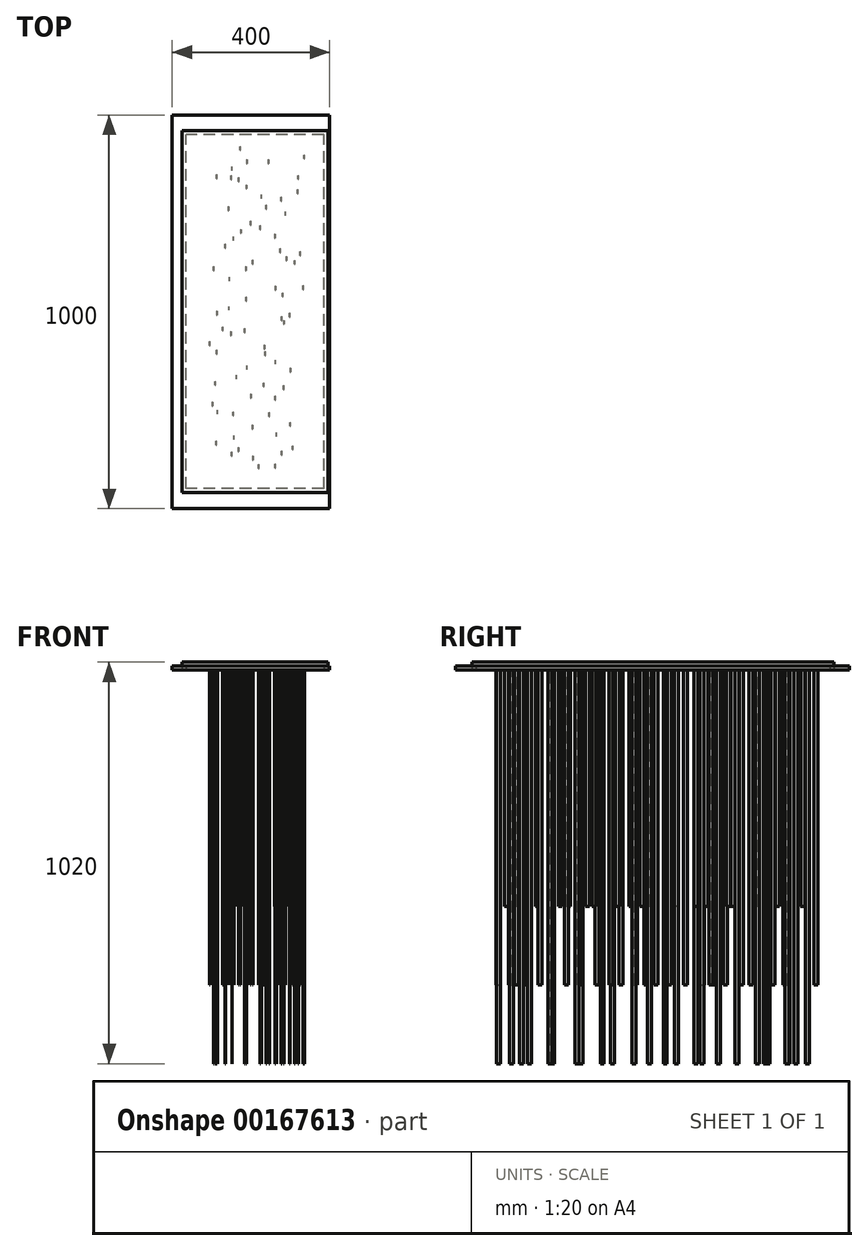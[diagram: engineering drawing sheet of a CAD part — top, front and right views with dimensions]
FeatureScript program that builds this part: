
annotation { "Feature Type Name" : "Feature", "Feature Type Description" : "" }
export const myFeature = defineFeature(function(context is Context, id is Id, definition is map)
    precondition{}
    {
        {
            var Q0;
            Q0=qCreatedBy(makeId("Top.planeOp"),FACE);
            var sketch = newSketch(context, id + "F0", { "sketchPlane" : qUnion([Q0])});
            skLineSegment(sketch, "E0.bottom", {"start": v(225, -500) * mm, "end": v(-225, -500) * mm});
            skLineSegment(sketch, "E0.top", {"start": v(225, 500) * mm, "end": v(-225, 500) * mm});
            skLineSegment(sketch, "E0.left", {"start": v(225, -500) * mm, "end": v(225, 500) * mm});
            skLineSegment(sketch, "E0.right", {"start": v(-225, -500) * mm, "end": v(-225, 500) * mm});
            skPoint(sketch, "E0.middle", {"position": v(0, 0) * mm});
            skSolve(sketch);
        }
        {
            var Q0;
            Q0=qCreatedBy(makeId("Top.planeOp"),FACE);
            var sketch = newSketch(context, id + "F1", { "sketchPlane" : qUnion([Q0])});
            skLineSegment(sketch, "E1.bottom", {"start": v(97.67, -13.3) * mm, "end": v(98.67, -13.3) * mm});
            skLineSegment(sketch, "E1.top", {"start": v(97.67, -3.3) * mm, "end": v(98.67, -3.3) * mm});
            skLineSegment(sketch, "E1.left", {"start": v(97.67, -13.3) * mm, "end": v(97.67, -3.3) * mm});
            skLineSegment(sketch, "E1.right", {"start": v(98.67, -13.3) * mm, "end": v(98.67, -3.3) * mm});
            skLineSegment(sketch, "E2.bottom", {"start": v(-15.97, -52.02) * mm, "end": v(-14.97, -52.02) * mm});
            skLineSegment(sketch, "E2.top", {"start": v(-15.97, -42.02) * mm, "end": v(-14.97, -42.02) * mm});
            skLineSegment(sketch, "E2.left", {"start": v(-15.97, -52.02) * mm, "end": v(-15.97, -42.02) * mm});
            skLineSegment(sketch, "E2.right", {"start": v(-14.97, -52.02) * mm, "end": v(-14.97, -42.02) * mm});
            skLineSegment(sketch, "E3.bottom", {"start": v(-12.36, 27.2) * mm, "end": v(-11.36, 27.2) * mm});
            skLineSegment(sketch, "E3.top", {"start": v(-12.36, 37.2) * mm, "end": v(-11.36, 37.2) * mm});
            skLineSegment(sketch, "E3.left", {"start": v(-12.36, 27.2) * mm, "end": v(-12.36, 37.2) * mm});
            skLineSegment(sketch, "E3.right", {"start": v(-11.36, 27.2) * mm, "end": v(-11.36, 37.2) * mm});
            skLineSegment(sketch, "E4.bottom", {"start": v(-91.45, -186.35) * mm, "end": v(-90.45, -186.35) * mm});
            skLineSegment(sketch, "E4.top", {"start": v(-91.45, -176.35) * mm, "end": v(-90.45, -176.35) * mm});
            skLineSegment(sketch, "E4.left", {"start": v(-91.45, -186.35) * mm, "end": v(-91.45, -176.35) * mm});
            skLineSegment(sketch, "E4.right", {"start": v(-90.45, -186.35) * mm, "end": v(-90.45, -176.35) * mm});
            skLineSegment(sketch, "E5.bottom", {"start": v(-87.84, -107.13) * mm, "end": v(-86.84, -107.13) * mm});
            skLineSegment(sketch, "E5.top", {"start": v(-87.84, -97.13) * mm, "end": v(-86.84, -97.13) * mm});
            skLineSegment(sketch, "E5.left", {"start": v(-87.84, -107.13) * mm, "end": v(-87.84, -97.13) * mm});
            skLineSegment(sketch, "E5.right", {"start": v(-86.84, -107.13) * mm, "end": v(-86.84, -97.13) * mm});
            skLineSegment(sketch, "E6.bottom", {"start": v(83.14, -197.41) * mm, "end": v(84.14, -197.41) * mm});
            skLineSegment(sketch, "E6.top", {"start": v(83.14, -187.41) * mm, "end": v(84.14, -187.41) * mm});
            skLineSegment(sketch, "E6.left", {"start": v(83.14, -197.41) * mm, "end": v(83.14, -187.41) * mm});
            skLineSegment(sketch, "E6.right", {"start": v(84.14, -197.41) * mm, "end": v(84.14, -187.41) * mm});
            skLineSegment(sketch, "E7.bottom", {"start": v(61.74, -132.83) * mm, "end": v(62.74, -132.83) * mm});
            skLineSegment(sketch, "E7.top", {"start": v(61.74, -122.83) * mm, "end": v(62.74, -122.83) * mm});
            skLineSegment(sketch, "E7.left", {"start": v(61.74, -132.83) * mm, "end": v(61.74, -122.83) * mm});
            skLineSegment(sketch, "E7.right", {"start": v(62.74, -132.83) * mm, "end": v(62.74, -122.83) * mm});
            skLineSegment(sketch, "E8.bottom", {"start": v(132.38, 56.37) * mm, "end": v(133.38, 56.37) * mm});
            skLineSegment(sketch, "E8.top", {"start": v(132.38, 66.37) * mm, "end": v(133.38, 66.37) * mm});
            skLineSegment(sketch, "E8.left", {"start": v(132.38, 56.37) * mm, "end": v(132.38, 66.37) * mm});
            skLineSegment(sketch, "E8.right", {"start": v(133.38, 56.37) * mm, "end": v(133.38, 66.37) * mm});
            skLineSegment(sketch, "E9.bottom", {"start": v(110.98, 120.95) * mm, "end": v(111.98, 120.95) * mm});
            skLineSegment(sketch, "E9.top", {"start": v(110.98, 130.95) * mm, "end": v(111.98, 130.95) * mm});
            skLineSegment(sketch, "E9.left", {"start": v(110.98, 120.95) * mm, "end": v(110.98, 130.95) * mm});
            skLineSegment(sketch, "E9.right", {"start": v(111.98, 120.95) * mm, "end": v(111.98, 130.95) * mm});
            skLineSegment(sketch, "E10.bottom", {"start": v(-95.04, 104.89) * mm, "end": v(-94.04, 104.89) * mm});
            skLineSegment(sketch, "E10.top", {"start": v(-95.04, 114.89) * mm, "end": v(-94.04, 114.89) * mm});
            skLineSegment(sketch, "E10.left", {"start": v(-95.04, 104.89) * mm, "end": v(-95.04, 114.89) * mm});
            skLineSegment(sketch, "E10.right", {"start": v(-94.04, 104.89) * mm, "end": v(-94.04, 114.89) * mm});
            skLineSegment(sketch, "E11.bottom", {"start": v(-65.86, 162.25) * mm, "end": v(-64.86, 162.25) * mm});
            skLineSegment(sketch, "E11.top", {"start": v(-65.86, 172.25) * mm, "end": v(-64.86, 172.25) * mm});
            skLineSegment(sketch, "E11.left", {"start": v(-65.86, 162.25) * mm, "end": v(-65.86, 172.25) * mm});
            skLineSegment(sketch, "E11.right", {"start": v(-64.86, 162.25) * mm, "end": v(-64.86, 172.25) * mm});
            skLineSegment(sketch, "E12.bottom", {"start": v(38.54, 261.3) * mm, "end": v(39.54, 261.3) * mm});
            skLineSegment(sketch, "E12.top", {"start": v(38.54, 271.3) * mm, "end": v(39.54, 271.3) * mm});
            skLineSegment(sketch, "E12.left", {"start": v(38.54, 261.3) * mm, "end": v(38.54, 271.3) * mm});
            skLineSegment(sketch, "E12.right", {"start": v(39.54, 261.3) * mm, "end": v(39.54, 271.3) * mm});
            skLineSegment(sketch, "E13.bottom", {"start": v(22.57, 209.28) * mm, "end": v(23.57, 209.28) * mm});
            skLineSegment(sketch, "E13.top", {"start": v(22.57, 219.28) * mm, "end": v(23.57, 219.28) * mm});
            skLineSegment(sketch, "E13.left", {"start": v(22.57, 209.28) * mm, "end": v(22.57, 219.28) * mm});
            skLineSegment(sketch, "E13.right", {"start": v(23.57, 209.28) * mm, "end": v(23.57, 219.28) * mm});
            skLineSegment(sketch, "E14.bottom", {"start": v(26.18, 288.5) * mm, "end": v(27.18, 288.5) * mm});
            skLineSegment(sketch, "E14.top", {"start": v(26.18, 298.5) * mm, "end": v(27.18, 298.5) * mm});
            skLineSegment(sketch, "E14.left", {"start": v(26.18, 288.5) * mm, "end": v(26.18, 298.5) * mm});
            skLineSegment(sketch, "E14.right", {"start": v(27.18, 288.5) * mm, "end": v(27.18, 298.5) * mm});
            skLineSegment(sketch, "E15.bottom", {"start": v(76.76, 281.29) * mm, "end": v(77.76, 281.29) * mm});
            skLineSegment(sketch, "E15.top", {"start": v(76.76, 291.29) * mm, "end": v(77.76, 291.29) * mm});
            skLineSegment(sketch, "E15.left", {"start": v(76.76, 281.29) * mm, "end": v(76.76, 291.29) * mm});
            skLineSegment(sketch, "E15.right", {"start": v(77.76, 281.29) * mm, "end": v(77.76, 291.29) * mm});
            skLineSegment(sketch, "E16.bottom", {"start": v(-87.04, 339.08) * mm, "end": v(-86.04, 339.08) * mm});
            skLineSegment(sketch, "E16.top", {"start": v(-87.04, 349.08) * mm, "end": v(-86.04, 349.08) * mm});
            skLineSegment(sketch, "E16.left", {"start": v(-87.04, 339.08) * mm, "end": v(-87.04, 349.08) * mm});
            skLineSegment(sketch, "E16.right", {"start": v(-86.04, 339.08) * mm, "end": v(-86.04, 349.08) * mm});
            skLineSegment(sketch, "E17.bottom", {"start": v(-48.82, 359.07) * mm, "end": v(-47.82, 359.07) * mm});
            skLineSegment(sketch, "E17.top", {"start": v(-48.82, 369.07) * mm, "end": v(-47.82, 369.07) * mm});
            skLineSegment(sketch, "E17.left", {"start": v(-48.82, 359.07) * mm, "end": v(-48.82, 369.07) * mm});
            skLineSegment(sketch, "E17.right", {"start": v(-47.82, 359.07) * mm, "end": v(-47.82, 369.07) * mm});
            skLineSegment(sketch, "E18.bottom", {"start": v(135.22, 388.86) * mm, "end": v(136.22, 388.86) * mm});
            skLineSegment(sketch, "E18.top", {"start": v(135.22, 398.86) * mm, "end": v(136.22, 398.86) * mm});
            skLineSegment(sketch, "E18.left", {"start": v(135.22, 388.86) * mm, "end": v(135.22, 398.86) * mm});
            skLineSegment(sketch, "E18.right", {"start": v(136.22, 388.86) * mm, "end": v(136.22, 398.86) * mm});
            skLineSegment(sketch, "E19.bottom", {"start": v(119.26, 336.85) * mm, "end": v(120.26, 336.85) * mm});
            skLineSegment(sketch, "E19.top", {"start": v(119.26, 346.85) * mm, "end": v(120.26, 346.85) * mm});
            skLineSegment(sketch, "E19.left", {"start": v(119.26, 336.85) * mm, "end": v(119.26, 346.85) * mm});
            skLineSegment(sketch, "E19.right", {"start": v(120.26, 336.85) * mm, "end": v(120.26, 346.85) * mm});
            skLineSegment(sketch, "E20.bottom", {"start": v(46.01, -265.67) * mm, "end": v(47.01, -265.67) * mm});
            skLineSegment(sketch, "E20.top", {"start": v(46.01, -255.67) * mm, "end": v(47.01, -255.67) * mm});
            skLineSegment(sketch, "E20.left", {"start": v(46.01, -265.67) * mm, "end": v(46.01, -255.67) * mm});
            skLineSegment(sketch, "E20.right", {"start": v(47.01, -265.67) * mm, "end": v(47.01, -255.67) * mm});
            skLineSegment(sketch, "E21.bottom", {"start": v(-89.07, -338.41) * mm, "end": v(-88.07, -338.41) * mm});
            skLineSegment(sketch, "E21.top", {"start": v(-89.07, -328.41) * mm, "end": v(-88.07, -328.41) * mm});
            skLineSegment(sketch, "E21.left", {"start": v(-89.07, -338.41) * mm, "end": v(-89.07, -328.41) * mm});
            skLineSegment(sketch, "E21.right", {"start": v(-88.07, -338.41) * mm, "end": v(-88.07, -328.41) * mm});
            skLineSegment(sketch, "E22.bottom", {"start": v(-85.46, -259.2) * mm, "end": v(-84.46, -259.2) * mm});
            skLineSegment(sketch, "E22.top", {"start": v(-85.46, -249.2) * mm, "end": v(-84.46, -249.2) * mm});
            skLineSegment(sketch, "E22.left", {"start": v(-85.46, -259.2) * mm, "end": v(-85.46, -249.2) * mm});
            skLineSegment(sketch, "E22.right", {"start": v(-84.46, -259.2) * mm, "end": v(-84.46, -249.2) * mm});
            skLineSegment(sketch, "E23.bottom", {"start": v(77.32, -363.16) * mm, "end": v(78.32, -363.16) * mm});
            skLineSegment(sketch, "E23.top", {"start": v(77.32, -353.16) * mm, "end": v(78.32, -353.16) * mm});
            skLineSegment(sketch, "E23.left", {"start": v(77.32, -363.16) * mm, "end": v(77.32, -353.16) * mm});
            skLineSegment(sketch, "E23.right", {"start": v(78.32, -363.16) * mm, "end": v(78.32, -353.16) * mm});
            skLineSegment(sketch, "E24.bottom", {"start": v(60.75, -396.29) * mm, "end": v(61.75, -396.29) * mm});
            skLineSegment(sketch, "E24.top", {"start": v(60.75, -386.29) * mm, "end": v(61.75, -386.29) * mm});
            skLineSegment(sketch, "E24.left", {"start": v(60.75, -396.29) * mm, "end": v(60.75, -386.29) * mm});
            skLineSegment(sketch, "E24.right", {"start": v(61.75, -396.29) * mm, "end": v(61.75, -386.29) * mm});
            skLineSegment(sketch, "E25.bottom", {"start": v(64.36, -317.06) * mm, "end": v(65.36, -317.06) * mm});
            skLineSegment(sketch, "E25.top", {"start": v(64.36, -307.06) * mm, "end": v(65.36, -307.06) * mm});
            skLineSegment(sketch, "E25.left", {"start": v(64.36, -317.06) * mm, "end": v(64.36, -307.06) * mm});
            skLineSegment(sketch, "E25.right", {"start": v(65.36, -317.06) * mm, "end": v(65.36, -307.06) * mm});
            skSolve(sketch);
        }
        {
            var Q0;
            Q0=makeQuery(id+"F1.imprint","IMPRINT",FACE,{"disambiguationData":[TD([[makeQuery(id+"F1.imprint","IMPRINT",EDGE,{"derivedFrom":sQuery(id+"F1.wireOp",EDGE,"0d04070f-8b83-4f4a-be27-bcda2ea6e18e.bottom")}),1.0]])]});
            var Q1;
            Q1=makeQuery(id+"F1.imprint","IMPRINT",FACE,{"disambiguationData":[TD([[makeQuery(id+"F1.imprint","IMPRINT",EDGE,{"derivedFrom":sQuery(id+"F1.wireOp",EDGE,"4a674c8a-05de-4ed7-8cc2-5f2642e71b03.bottom")}),1.0]])]});
            var Q2;
            Q2=makeQuery(id+"F1.imprint","IMPRINT",FACE,{"disambiguationData":[TD([[makeQuery(id+"F1.imprint","IMPRINT",EDGE,{"derivedFrom":sQuery(id+"F1.wireOp",EDGE,"E18.bottom")}),1.0]])]});
            var Q3;
            Q3=makeQuery(id+"F1.imprint","IMPRINT",FACE,{"disambiguationData":[TD([[makeQuery(id+"F1.imprint","IMPRINT",EDGE,{"derivedFrom":sQuery(id+"F1.wireOp",EDGE,"3bdfd535-c372-4a8e-893e-25be1731da4d.bottom")}),1.0]])]});
            var Q4;
            Q4=makeQuery(id+"F1.imprint","IMPRINT",FACE,{"disambiguationData":[TD([[makeQuery(id+"F1.imprint","IMPRINT",EDGE,{"derivedFrom":sQuery(id+"F1.wireOp",EDGE,"E19.bottom")}),1.0]])]});
            var Q5;
            Q5=makeQuery(id+"F1.imprint","IMPRINT",FACE,{"disambiguationData":[TD([[makeQuery(id+"F1.imprint","IMPRINT",EDGE,{"derivedFrom":sQuery(id+"F1.wireOp",EDGE,"e37778a0-9165-4534-8185-db5a5166a639.bottom")}),1.0]])]});
            var Q6;
            Q6=makeQuery(id+"F1.imprint","IMPRINT",FACE,{"disambiguationData":[TD([[makeQuery(id+"F1.imprint","IMPRINT",EDGE,{"derivedFrom":sQuery(id+"F1.wireOp",EDGE,"E17.bottom")}),1.0]])]});
            var Q7;
            Q7=makeQuery(id+"F1.imprint","IMPRINT",FACE,{"disambiguationData":[TD([[makeQuery(id+"F1.imprint","IMPRINT",EDGE,{"derivedFrom":sQuery(id+"F1.wireOp",EDGE,"E16.bottom")}),1.0]])]});
            var Q8;
            Q8=makeQuery(id+"F1.imprint","IMPRINT",FACE,{"disambiguationData":[TD([[makeQuery(id+"F1.imprint","IMPRINT",EDGE,{"derivedFrom":sQuery(id+"F1.wireOp",EDGE,"a969c94d-df2b-45b1-a30c-0c96835f0a28.bottom")}),1.0]])]});
            var Q9;
            Q9=makeQuery(id+"F1.imprint","IMPRINT",FACE,{"disambiguationData":[TD([[makeQuery(id+"F1.imprint","IMPRINT",EDGE,{"derivedFrom":sQuery(id+"F1.wireOp",EDGE,"0afe55c9-5bc2-4576-8854-4dd6c9ddc86a.bottom")}),1.0]])]});
            var Q10;
            Q10=makeQuery(id+"F1.imprint","IMPRINT",FACE,{"disambiguationData":[TD([[makeQuery(id+"F1.imprint","IMPRINT",EDGE,{"derivedFrom":sQuery(id+"F1.wireOp",EDGE,"E15.bottom")}),1.0]])]});
            var Q11;
            Q11=makeQuery(id+"F1.imprint","IMPRINT",FACE,{"disambiguationData":[TD([[makeQuery(id+"F1.imprint","IMPRINT",EDGE,{"derivedFrom":sQuery(id+"F1.wireOp",EDGE,"E14.bottom")}),1.0]])]});
            var Q12;
            Q12=makeQuery(id+"F1.imprint","IMPRINT",FACE,{"disambiguationData":[TD([[makeQuery(id+"F1.imprint","IMPRINT",EDGE,{"derivedFrom":sQuery(id+"F1.wireOp",EDGE,"E12.bottom")}),1.0]])]});
            var Q13;
            Q13=makeQuery(id+"F1.imprint","IMPRINT",FACE,{"disambiguationData":[TD([[makeQuery(id+"F1.imprint","IMPRINT",EDGE,{"derivedFrom":sQuery(id+"F1.wireOp",EDGE,"979c37d6-b26a-4ecc-b853-e4a640f24a5b.bottom")}),1.0]])]});
            var Q14;
            Q14=makeQuery(id+"F1.imprint","IMPRINT",FACE,{"disambiguationData":[TD([[makeQuery(id+"F1.imprint","IMPRINT",EDGE,{"derivedFrom":sQuery(id+"F1.wireOp",EDGE,"E13.bottom")}),1.0]])]});
            var Q15;
            Q15=makeQuery(id+"F1.imprint","IMPRINT",FACE,{"disambiguationData":[TD([[makeQuery(id+"F1.imprint","IMPRINT",EDGE,{"derivedFrom":sQuery(id+"F1.wireOp",EDGE,"7d292e70-048c-4178-bbf2-0c1e53966c0b.bottom")}),1.0]])]});
            var Q16;
            Q16=makeQuery(id+"F1.imprint","IMPRINT",FACE,{"disambiguationData":[TD([[makeQuery(id+"F1.imprint","IMPRINT",EDGE,{"derivedFrom":sQuery(id+"F1.wireOp",EDGE,"E11.bottom")}),1.0]])]});
            var Q17;
            Q17=makeQuery(id+"F1.imprint","IMPRINT",FACE,{"disambiguationData":[TD([[makeQuery(id+"F1.imprint","IMPRINT",EDGE,{"derivedFrom":sQuery(id+"F1.wireOp",EDGE,"7692440d-4202-4584-bad4-5c0328639483.bottom")}),1.0]])]});
            var Q18;
            Q18=makeQuery(id+"F1.imprint","IMPRINT",FACE,{"disambiguationData":[TD([[makeQuery(id+"F1.imprint","IMPRINT",EDGE,{"derivedFrom":sQuery(id+"F1.wireOp",EDGE,"E10.bottom")}),1.0]])]});
            var Q19;
            Q19=makeQuery(id+"F1.imprint","IMPRINT",FACE,{"disambiguationData":[TD([[makeQuery(id+"F1.imprint","IMPRINT",EDGE,{"derivedFrom":sQuery(id+"F1.wireOp",EDGE,"8622bb89-44d4-4816-ba5b-b360be4d14c9.bottom")}),1.0]])]});
            var Q20;
            Q20=makeQuery(id+"F1.imprint","IMPRINT",FACE,{"disambiguationData":[TD([[makeQuery(id+"F1.imprint","IMPRINT",EDGE,{"derivedFrom":sQuery(id+"F1.wireOp",EDGE,"E9.bottom")}),1.0]])]});
            var Q21;
            Q21=makeQuery(id+"F1.imprint","IMPRINT",FACE,{"disambiguationData":[TD([[makeQuery(id+"F1.imprint","IMPRINT",EDGE,{"derivedFrom":sQuery(id+"F1.wireOp",EDGE,"befe3600-d2c4-417b-abc3-b6d777ba2422.bottom")}),1.0]])]});
            var Q22;
            Q22=makeQuery(id+"F1.imprint","IMPRINT",FACE,{"disambiguationData":[TD([[makeQuery(id+"F1.imprint","IMPRINT",EDGE,{"derivedFrom":sQuery(id+"F1.wireOp",EDGE,"72c611a4-0e0b-4f80-8393-7aa807bcaec6.bottom")}),1.0]])]});
            var Q23;
            Q23=makeQuery(id+"F1.imprint","IMPRINT",FACE,{"disambiguationData":[TD([[makeQuery(id+"F1.imprint","IMPRINT",EDGE,{"derivedFrom":sQuery(id+"F1.wireOp",EDGE,"E8.bottom")}),1.0]])]});
            var Q24;
            Q24=makeQuery(id+"F1.imprint","IMPRINT",FACE,{"disambiguationData":[TD([[makeQuery(id+"F1.imprint","IMPRINT",EDGE,{"derivedFrom":sQuery(id+"F1.wireOp",EDGE,"c4f17c63-c593-4075-a2ab-d9e853c5fc45.bottom")}),1.0]])]});
            var Q25;
            Q25=makeQuery(id+"F1.imprint","IMPRINT",FACE,{"disambiguationData":[TD([[makeQuery(id+"F1.imprint","IMPRINT",EDGE,{"derivedFrom":sQuery(id+"F1.wireOp",EDGE,"426057d1-b418-44bf-8107-993e25366d78.bottom")}),1.0]])]});
            var Q26;
            Q26=makeQuery(id+"F1.imprint","IMPRINT",FACE,{"disambiguationData":[TD([[makeQuery(id+"F1.imprint","IMPRINT",EDGE,{"derivedFrom":sQuery(id+"F1.wireOp",EDGE,"E3.bottom")}),1.0]])]});
            var Q27;
            Q27=makeQuery(id+"F1.imprint","IMPRINT",FACE,{"disambiguationData":[TD([[makeQuery(id+"F1.imprint","IMPRINT",EDGE,{"derivedFrom":sQuery(id+"F1.wireOp",EDGE,"wPaIKOaS-dw31-QlfZ-ihIT-eXd3RULe7Bit.bottom")}),1.0]])]});
            var Q28;
            Q28=makeQuery(id+"F1.imprint","IMPRINT",FACE,{"disambiguationData":[TD([[makeQuery(id+"F1.imprint","IMPRINT",EDGE,{"derivedFrom":sQuery(id+"F1.wireOp",EDGE,"E1.bottom")}),1.0]])]});
            var Q29;
            Q29=makeQuery(id+"F1.imprint","IMPRINT",FACE,{"disambiguationData":[TD([[makeQuery(id+"F1.imprint","IMPRINT",EDGE,{"derivedFrom":sQuery(id+"F1.wireOp",EDGE,"E2.bottom")}),1.0]])]});
            var Q30;
            Q30=makeQuery(id+"F1.imprint","IMPRINT",FACE,{"disambiguationData":[TD([[makeQuery(id+"F1.imprint","IMPRINT",EDGE,{"derivedFrom":sQuery(id+"F1.wireOp",EDGE,"E5.bottom")}),1.0]])]});
            var Q31;
            Q31=makeQuery(id+"F1.imprint","IMPRINT",FACE,{"disambiguationData":[TD([[makeQuery(id+"F1.imprint","IMPRINT",EDGE,{"derivedFrom":sQuery(id+"F1.wireOp",EDGE,"bc6d5639-2fdf-4032-8914-32b7b8087d86.bottom")}),1.0]])]});
            var Q32;
            Q32=makeQuery(id+"F1.imprint","IMPRINT",FACE,{"disambiguationData":[TD([[makeQuery(id+"F1.imprint","IMPRINT",EDGE,{"derivedFrom":sQuery(id+"F1.wireOp",EDGE,"e741ae37-8342-450e-ab9f-a91f64156133.bottom")}),1.0]])]});
            var Q33;
            Q33=makeQuery(id+"F1.imprint","IMPRINT",FACE,{"disambiguationData":[TD([[makeQuery(id+"F1.imprint","IMPRINT",EDGE,{"derivedFrom":sQuery(id+"F1.wireOp",EDGE,"6b1ab266-fcd8-4207-968b-38e29c2719eb.bottom")}),1.0]])]});
            var Q34;
            Q34=makeQuery(id+"F1.imprint","IMPRINT",FACE,{"disambiguationData":[TD([[makeQuery(id+"F1.imprint","IMPRINT",EDGE,{"derivedFrom":sQuery(id+"F1.wireOp",EDGE,"E4.bottom")}),1.0]])]});
            var Q35;
            Q35=makeQuery(id+"F1.imprint","IMPRINT",FACE,{"disambiguationData":[TD([[makeQuery(id+"F1.imprint","IMPRINT",EDGE,{"derivedFrom":sQuery(id+"F1.wireOp",EDGE,"E7.bottom")}),1.0]])]});
            var Q36;
            Q36=makeQuery(id+"F1.imprint","IMPRINT",FACE,{"disambiguationData":[TD([[makeQuery(id+"F1.imprint","IMPRINT",EDGE,{"derivedFrom":sQuery(id+"F1.wireOp",EDGE,"1e3ae946-030e-43b2-b625-1525fa5efbff.bottom")}),1.0]])]});
            var Q37;
            Q37=makeQuery(id+"F1.imprint","IMPRINT",FACE,{"disambiguationData":[TD([[makeQuery(id+"F1.imprint","IMPRINT",EDGE,{"derivedFrom":sQuery(id+"F1.wireOp",EDGE,"E6.bottom")}),1.0]])]});
            var Q38;
            Q38=makeQuery(id+"F1.imprint","IMPRINT",FACE,{"disambiguationData":[TD([[makeQuery(id+"F1.imprint","IMPRINT",EDGE,{"derivedFrom":sQuery(id+"F1.wireOp",EDGE,"5dee2036-e38d-4daf-a4ac-c73f742bd943.bottom")}),1.0]])]});
            var Q39;
            Q39=makeQuery(id+"F1.imprint","IMPRINT",FACE,{"disambiguationData":[TD([[makeQuery(id+"F1.imprint","IMPRINT",EDGE,{"derivedFrom":sQuery(id+"F1.wireOp",EDGE,"fcc809ca-fb7e-4bae-9142-1bac50f077b9.bottom")}),1.0]])]});
            var Q40;
            Q40=makeQuery(id+"F1.imprint","IMPRINT",FACE,{"disambiguationData":[TD([[makeQuery(id+"F1.imprint","IMPRINT",EDGE,{"derivedFrom":sQuery(id+"F1.wireOp",EDGE,"E23.bottom")}),1.0]])]});
            var Q41;
            Q41=makeQuery(id+"F1.imprint","IMPRINT",FACE,{"disambiguationData":[TD([[makeQuery(id+"F1.imprint","IMPRINT",EDGE,{"derivedFrom":sQuery(id+"F1.wireOp",EDGE,"E25.bottom")}),1.0]])]});
            var Q42;
            Q42=makeQuery(id+"F1.imprint","IMPRINT",FACE,{"disambiguationData":[TD([[makeQuery(id+"F1.imprint","IMPRINT",EDGE,{"derivedFrom":sQuery(id+"F1.wireOp",EDGE,"ea3d2090-3f77-4217-bbf3-f4d39c6890dc.bottom")}),1.0]])]});
            var Q43;
            Q43=makeQuery(id+"F1.imprint","IMPRINT",FACE,{"disambiguationData":[TD([[makeQuery(id+"F1.imprint","IMPRINT",EDGE,{"derivedFrom":sQuery(id+"F1.wireOp",EDGE,"E24.bottom")}),1.0]])]});
            var Q44;
            Q44=makeQuery(id+"F1.imprint","IMPRINT",FACE,{"disambiguationData":[TD([[makeQuery(id+"F1.imprint","IMPRINT",EDGE,{"derivedFrom":sQuery(id+"F1.wireOp",EDGE,"c863d00d-ee32-4f43-a828-3206477b2538.bottom")}),1.0]])]});
            var Q45;
            Q45=makeQuery(id+"F1.imprint","IMPRINT",FACE,{"disambiguationData":[TD([[makeQuery(id+"F1.imprint","IMPRINT",EDGE,{"derivedFrom":sQuery(id+"F1.wireOp",EDGE,"E21.bottom")}),1.0]])]});
            var Q46;
            Q46=makeQuery(id+"F1.imprint","IMPRINT",FACE,{"disambiguationData":[TD([[makeQuery(id+"F1.imprint","IMPRINT",EDGE,{"derivedFrom":sQuery(id+"F1.wireOp",EDGE,"E20.bottom")}),1.0]])]});
            var Q47;
            Q47=makeQuery(id+"F1.imprint","IMPRINT",FACE,{"disambiguationData":[TD([[makeQuery(id+"F1.imprint","IMPRINT",EDGE,{"derivedFrom":sQuery(id+"F1.wireOp",EDGE,"E22.bottom")}),1.0]])]});
            var Q48;
            Q48=makeQuery(id+"F1.imprint","IMPRINT",FACE,{"disambiguationData":[TD([[makeQuery(id+"F1.imprint","IMPRINT",EDGE,{"derivedFrom":sQuery(id+"F1.wireOp",EDGE,"d74cf85c-c818-4ad0-9b48-6eb2aca7f4b0.bottom")}),1.0]])]});
            var Q49;
            Q49=makeQuery(id+"F1.imprint","IMPRINT",FACE,{"disambiguationData":[TD([[makeQuery(id+"F1.imprint","IMPRINT",EDGE,{"derivedFrom":sQuery(id+"F1.wireOp",EDGE,"4c03ad0b-09ab-4c6e-8477-7c7ecc1090b5.bottom")}),1.0]])]});
            extrude(context, id + "F2", {"entities" : qUnion([Q0, Q1, Q2, Q3, Q4, Q5, Q6, Q7, Q8, Q9, Q10, Q11, Q12, Q13, Q14, Q15, Q16, Q17, Q18, Q19, Q20, Q21, Q22, Q23, Q24, Q25, Q26, Q27, Q28, Q29, Q30, Q31, Q32, Q33, Q34, Q35, Q36, Q37, Q38, Q39, Q40, Q41, Q42, Q43, Q44, Q45, Q46, Q47, Q48, Q49]), "oppositeDirection" : true, "depth" : 1000 * mm});
        }
        {
            var Q0;
            Q0=qCreatedBy(makeId("Top.planeOp"),FACE);
            var sketch = newSketch(context, id + "F3", { "sketchPlane" : qUnion([Q0])});
            skLineSegment(sketch, "E26.MirrorCS", {"start": v(-58.05, 257.07) * mm, "end": v(-57.05, 257.07) * mm});
            skLineSegment(sketch, "E27.MirrorCS", {"start": v(3.6, -376.19) * mm, "end": v(4.6, -376.19) * mm});
            skLineSegment(sketch, "E28.MirrorCS", {"start": v(-58.05, 267.07) * mm, "end": v(-57.05, 267.07) * mm});
            skLineSegment(sketch, "E29.MirrorCS", {"start": v(3.6, -366.19) * mm, "end": v(4.6, -366.19) * mm});
            skLineSegment(sketch, "E30.MirrorCS", {"start": v(43.27, 387.28) * mm, "end": v(44.27, 387.28) * mm});
            skLineSegment(sketch, "E31.MirrorCS", {"start": v(-0.6, -208.62) * mm, "end": v(0.4, -208.62) * mm});
            skLineSegment(sketch, "E32.MirrorCS", {"start": v(43.27, 377.28) * mm, "end": v(44.27, 377.28) * mm});
            skLineSegment(sketch, "E33.MirrorCS", {"start": v(-0.6, -218.62) * mm, "end": v(0.4, -218.62) * mm});
            skLineSegment(sketch, "E34.MirrorCS", {"start": v(-11.27, 376.41) * mm, "end": v(-10.27, 376.41) * mm});
            skLineSegment(sketch, "E35.MirrorCS", {"start": v(82.77, -31.45) * mm, "end": v(83.77, -31.45) * mm});
            skLineSegment(sketch, "E36.MirrorCS", {"start": v(-11.27, 386.41) * mm, "end": v(-10.27, 386.41) * mm});
            skLineSegment(sketch, "E37.MirrorCS", {"start": v(82.77, -21.45) * mm, "end": v(83.77, -21.45) * mm});
            skLineSegment(sketch, "E38.MirrorCS", {"start": v(-58.05, 267.07) * mm, "end": v(-58.05, 257.07) * mm});
            skLineSegment(sketch, "E39.MirrorCS", {"start": v(3.6, -366.19) * mm, "end": v(3.6, -376.19) * mm});
            skLineSegment(sketch, "E40.MirrorCS", {"start": v(43.27, 387.28) * mm, "end": v(43.27, 377.28) * mm});
            skLineSegment(sketch, "E41.MirrorCS", {"start": v(-0.6, -208.62) * mm, "end": v(-0.6, -218.62) * mm});
            skLineSegment(sketch, "E42.MirrorCS", {"start": v(99.7, -143.17) * mm, "end": v(100.7, -143.17) * mm});
            skLineSegment(sketch, "E43.MirrorCS", {"start": v(59.98, 198.07) * mm, "end": v(60.98, 198.07) * mm});
            skLineSegment(sketch, "E44.MirrorCS", {"start": v(59.98, 188.07) * mm, "end": v(60.98, 188.07) * mm});
            skLineSegment(sketch, "E45.MirrorCS", {"start": v(99.7, -153.17) * mm, "end": v(100.7, -153.17) * mm});
            skLineSegment(sketch, "E46.MirrorCS", {"start": v(83.77, -21.45) * mm, "end": v(83.77, -31.45) * mm});
            skLineSegment(sketch, "E47.MirrorCS", {"start": v(-10.27, 386.41) * mm, "end": v(-10.27, 376.41) * mm});
            skLineSegment(sketch, "E48.MirrorCS", {"start": v(-11.27, 386.41) * mm, "end": v(-11.27, 376.41) * mm});
            skLineSegment(sketch, "E49.MirrorCS", {"start": v(82.77, -21.45) * mm, "end": v(82.77, -31.45) * mm});
            skLineSegment(sketch, "E50.MirrorCS", {"start": v(-32.7, -344.3) * mm, "end": v(-31.7, -344.3) * mm});
            skLineSegment(sketch, "E51.MirrorCS", {"start": v(4.6, -366.19) * mm, "end": v(4.6, -376.19) * mm});
            skLineSegment(sketch, "E52.MirrorCS", {"start": v(-57.05, 267.07) * mm, "end": v(-57.05, 257.07) * mm});
            skLineSegment(sketch, "E53.MirrorCS", {"start": v(3.02, -287.84) * mm, "end": v(4.02, -287.84) * mm});
            skLineSegment(sketch, "E54.MirrorCS", {"start": v(44.27, 387.28) * mm, "end": v(44.27, 377.28) * mm});
            skLineSegment(sketch, "E55.MirrorCS", {"start": v(0.4, -208.62) * mm, "end": v(0.4, -218.62) * mm});
            skLineSegment(sketch, "E56.MirrorCS", {"start": v(60.98, 198.07) * mm, "end": v(60.98, 188.07) * mm});
            skLineSegment(sketch, "E57.MirrorCS", {"start": v(100.7, -143.17) * mm, "end": v(100.7, -153.17) * mm});
            skLineSegment(sketch, "E58.MirrorCS", {"start": v(59.98, 198.07) * mm, "end": v(59.98, 188.07) * mm});
            skLineSegment(sketch, "E59.MirrorCS", {"start": v(99.7, -143.17) * mm, "end": v(99.7, -153.17) * mm});
            skLineSegment(sketch, "E60.MirrorCS", {"start": v(-32.7, -344.3) * mm, "end": v(-32.7, -354.3) * mm});
            skLineSegment(sketch, "E61.MirrorCS", {"start": v(-32.7, -354.3) * mm, "end": v(-31.7, -354.3) * mm});
            skLineSegment(sketch, "E62.MirrorCS", {"start": v(3.02, -297.84) * mm, "end": v(4.02, -297.84) * mm});
            skLineSegment(sketch, "E63.MirrorCS", {"start": v(90.16, 140.71) * mm, "end": v(90.16, 130.71) * mm});
            skLineSegment(sketch, "E64.MirrorCS", {"start": v(89.16, 140.71) * mm, "end": v(89.16, 130.71) * mm});
            skLineSegment(sketch, "E65.MirrorCS", {"start": v(89.16, 130.71) * mm, "end": v(90.16, 130.71) * mm});
            skLineSegment(sketch, "E66.MirrorCS", {"start": v(89.16, 140.71) * mm, "end": v(90.16, 140.71) * mm});
            skLineSegment(sketch, "E67.MirrorCS", {"start": v(-31.7, -344.3) * mm, "end": v(-31.7, -354.3) * mm});
            skLineSegment(sketch, "E68.MirrorCS", {"start": v(4.02, -287.84) * mm, "end": v(4.02, -297.84) * mm});
            skLineSegment(sketch, "E69.MirrorCS", {"start": v(3.02, -287.84) * mm, "end": v(3.02, -297.84) * mm});
            skLineSegment(sketch, "E70.MirrorCS", {"start": v(-86.92, -8.23) * mm, "end": v(-85.92, -8.23) * mm});
            skLineSegment(sketch, "E71.MirrorCS", {"start": v(-86.92, 1.77) * mm, "end": v(-85.92, 1.77) * mm});
            skLineSegment(sketch, "E72.MirrorCS", {"start": v(-85.92, 1.77) * mm, "end": v(-85.92, -8.23) * mm});
            skLineSegment(sketch, "E73.MirrorCS", {"start": v(-86.92, 1.77) * mm, "end": v(-86.92, -8.23) * mm});
            skLineSegment(sketch, "E74.MirrorCS", {"start": v(-12.34, 312.8) * mm, "end": v(-11.34, 312.8) * mm});
            skLineSegment(sketch, "E75.MirrorCS", {"start": v(-12.34, 322.8) * mm, "end": v(-11.34, 322.8) * mm});
            skLineSegment(sketch, "E76.MirrorCS", {"start": v(-11.34, 322.8) * mm, "end": v(-11.34, 312.8) * mm});
            skLineSegment(sketch, "E77.MirrorCS", {"start": v(-12.34, 322.8) * mm, "end": v(-12.34, 312.8) * mm});
            skLineSegment(sketch, "E78.MirrorCS", {"start": v(-14.2, 104.97) * mm, "end": v(-13.2, 104.97) * mm});
            skLineSegment(sketch, "E79.MirrorCS", {"start": v(-14.2, 114.97) * mm, "end": v(-13.2, 114.97) * mm});
            skLineSegment(sketch, "E80.MirrorCS", {"start": v(-13.2, 114.97) * mm, "end": v(-13.2, 104.97) * mm});
            skLineSegment(sketch, "E81.MirrorCS", {"start": v(-14.2, 114.97) * mm, "end": v(-14.2, 104.97) * mm});
            skLineSegment(sketch, "E82.MirrorCS", {"start": v(-98.3, -239.38) * mm, "end": v(-97.3, -239.38) * mm});
            skLineSegment(sketch, "E83.MirrorCS", {"start": v(-98.3, -229.38) * mm, "end": v(-97.3, -229.38) * mm});
            skLineSegment(sketch, "E84.MirrorCS", {"start": v(-97.3, -229.38) * mm, "end": v(-97.3, -239.38) * mm});
            skLineSegment(sketch, "E85.MirrorCS", {"start": v(-98.3, -229.38) * mm, "end": v(-98.3, -239.38) * mm});
            skLineSegment(sketch, "E86.MirrorCS", {"start": v(33.07, -94) * mm, "end": v(34.07, -94) * mm});
            skLineSegment(sketch, "E87.MirrorCS", {"start": v(33.07, -84) * mm, "end": v(34.07, -84) * mm});
            skLineSegment(sketch, "E88.MirrorCS", {"start": v(34.07, -84) * mm, "end": v(34.07, -94) * mm});
            skLineSegment(sketch, "E89.MirrorCS", {"start": v(33.07, -84) * mm, "end": v(33.07, -94) * mm});
            skLineSegment(sketch, "E90.MirrorCS", {"start": v(-26.22, 199.63) * mm, "end": v(-25.22, 199.63) * mm});
            skLineSegment(sketch, "E91.MirrorCS", {"start": v(-26.22, 209.63) * mm, "end": v(-25.22, 209.63) * mm});
            skLineSegment(sketch, "E92.MirrorCS", {"start": v(-25.22, 209.63) * mm, "end": v(-25.22, 199.63) * mm});
            skLineSegment(sketch, "E93.MirrorCS", {"start": v(-26.22, 209.63) * mm, "end": v(-26.22, 199.63) * mm});
            skLineSegment(sketch, "E94.MirrorCS", {"start": v(-51.44, -59.67) * mm, "end": v(-50.44, -59.67) * mm});
            skLineSegment(sketch, "E95.MirrorCS", {"start": v(-51.44, -49.67) * mm, "end": v(-50.44, -49.67) * mm});
            skLineSegment(sketch, "E96.MirrorCS", {"start": v(-50.44, -49.67) * mm, "end": v(-50.44, -59.67) * mm});
            skLineSegment(sketch, "E97.MirrorCS", {"start": v(-51.44, -49.67) * mm, "end": v(-51.44, -59.67) * mm});
            skLineSegment(sketch, "E98.MirrorCS", {"start": v(61.6, 55.31) * mm, "end": v(62.6, 55.31) * mm});
            skLineSegment(sketch, "E99.MirrorCS", {"start": v(61.6, 65.31) * mm, "end": v(62.6, 65.31) * mm});
            skLineSegment(sketch, "E100.MirrorCS", {"start": v(62.6, 65.31) * mm, "end": v(62.6, 55.31) * mm});
            skLineSegment(sketch, "E101.MirrorCS", {"start": v(61.6, 65.31) * mm, "end": v(61.6, 55.31) * mm});
            skLineSegment(sketch, "E102.MirrorCS", {"start": v(-38.6, -170.42) * mm, "end": v(-37.6, -170.42) * mm});
            skLineSegment(sketch, "E103.MirrorCS", {"start": v(-38.6, -160.42) * mm, "end": v(-37.6, -160.42) * mm});
            skLineSegment(sketch, "E104.MirrorCS", {"start": v(-37.6, -160.42) * mm, "end": v(-37.6, -170.42) * mm});
            skLineSegment(sketch, "E105.MirrorCS", {"start": v(-38.6, -160.42) * mm, "end": v(-38.6, -170.42) * mm});
            skSolve(sketch);
        }
        {
            var Q0;
            Q0=qSketchRegion(id+"F3",true);
            extrude(context, id + "F4", {"entities" : qUnion([Q0]), "oppositeDirection" : true, "depth" : 600 * mm});
        }
        {
            var Q0;
            Q0=qCreatedBy(makeId("Top.planeOp"),FACE);
            var sketch = newSketch(context, id + "F5", { "sketchPlane" : qUnion([Q0])});
            skLineSegment(sketch, "E106.bottom", {"start": v(31.76, -190.2) * mm, "end": v(32.76, -190.2) * mm});
            skLineSegment(sketch, "E106.top", {"start": v(31.76, -180.2) * mm, "end": v(32.76, -180.2) * mm});
            skLineSegment(sketch, "E106.left", {"start": v(31.76, -190.2) * mm, "end": v(31.76, -180.2) * mm});
            skLineSegment(sketch, "E106.right", {"start": v(32.76, -190.2) * mm, "end": v(32.76, -180.2) * mm});
            skLineSegment(sketch, "E107.bottom", {"start": v(35.37, -110.98) * mm, "end": v(36.37, -110.98) * mm});
            skLineSegment(sketch, "E107.top", {"start": v(35.37, -100.98) * mm, "end": v(36.37, -100.98) * mm});
            skLineSegment(sketch, "E107.left", {"start": v(35.37, -110.98) * mm, "end": v(35.37, -100.98) * mm});
            skLineSegment(sketch, "E107.right", {"start": v(36.37, -110.98) * mm, "end": v(36.37, -100.98) * mm});
            skLineSegment(sketch, "E108.bottom", {"start": v(-43.72, -324.53) * mm, "end": v(-42.72, -324.53) * mm});
            skLineSegment(sketch, "E108.top", {"start": v(-43.72, -314.53) * mm, "end": v(-42.72, -314.53) * mm});
            skLineSegment(sketch, "E108.left", {"start": v(-43.72, -324.53) * mm, "end": v(-43.72, -314.53) * mm});
            skLineSegment(sketch, "E108.right", {"start": v(-42.72, -324.53) * mm, "end": v(-42.72, -314.53) * mm});
            skLineSegment(sketch, "E109.bottom", {"start": v(-45.26, -263.83) * mm, "end": v(-44.26, -263.83) * mm});
            skLineSegment(sketch, "E109.top", {"start": v(-45.26, -253.83) * mm, "end": v(-44.26, -253.83) * mm});
            skLineSegment(sketch, "E109.left", {"start": v(-45.26, -263.83) * mm, "end": v(-45.26, -253.83) * mm});
            skLineSegment(sketch, "E109.right", {"start": v(-44.26, -263.83) * mm, "end": v(-44.26, -253.83) * mm});
            skLineSegment(sketch, "E110.bottom", {"start": v(105.86, -350.24) * mm, "end": v(106.86, -350.24) * mm});
            skLineSegment(sketch, "E110.top", {"start": v(105.86, -340.24) * mm, "end": v(106.86, -340.24) * mm});
            skLineSegment(sketch, "E110.left", {"start": v(105.86, -350.24) * mm, "end": v(105.86, -340.24) * mm});
            skLineSegment(sketch, "E110.right", {"start": v(106.86, -350.24) * mm, "end": v(106.86, -340.24) * mm});
            skLineSegment(sketch, "E111.bottom", {"start": v(99.3, -290.5) * mm, "end": v(100.3, -290.5) * mm});
            skLineSegment(sketch, "E111.top", {"start": v(99.3, -280.5) * mm, "end": v(100.3, -280.5) * mm});
            skLineSegment(sketch, "E111.left", {"start": v(99.3, -290.5) * mm, "end": v(99.3, -280.5) * mm});
            skLineSegment(sketch, "E111.right", {"start": v(100.3, -290.5) * mm, "end": v(100.3, -280.5) * mm});
            skLineSegment(sketch, "E112.bottom", {"start": v(87.32, 244.9) * mm, "end": v(88.32, 244.9) * mm});
            skLineSegment(sketch, "E112.top", {"start": v(87.32, 254.9) * mm, "end": v(88.32, 254.9) * mm});
            skLineSegment(sketch, "E112.left", {"start": v(87.32, 244.9) * mm, "end": v(87.32, 254.9) * mm});
            skLineSegment(sketch, "E112.right", {"start": v(88.32, 244.9) * mm, "end": v(88.32, 254.9) * mm});
            skLineSegment(sketch, "E113.bottom", {"start": v(118.07, 301) * mm, "end": v(119.07, 301) * mm});
            skLineSegment(sketch, "E113.top", {"start": v(118.07, 311) * mm, "end": v(119.07, 311) * mm});
            skLineSegment(sketch, "E113.left", {"start": v(118.07, 301) * mm, "end": v(118.07, 311) * mm});
            skLineSegment(sketch, "E113.right", {"start": v(119.07, 301) * mm, "end": v(119.07, 311) * mm});
            skLineSegment(sketch, "E114.bottom", {"start": v(-56.36, 4.08) * mm, "end": v(-55.36, 4.08) * mm});
            skLineSegment(sketch, "E114.top", {"start": v(-56.36, 14.08) * mm, "end": v(-55.36, 14.08) * mm});
            skLineSegment(sketch, "E114.left", {"start": v(-56.36, 4.08) * mm, "end": v(-56.36, 14.08) * mm});
            skLineSegment(sketch, "E114.right", {"start": v(-55.36, 4.08) * mm, "end": v(-55.36, 14.08) * mm});
            skLineSegment(sketch, "E115.bottom", {"start": v(-72.33, -47.93) * mm, "end": v(-71.33, -47.93) * mm});
            skLineSegment(sketch, "E115.top", {"start": v(-72.33, -37.93) * mm, "end": v(-71.33, -37.93) * mm});
            skLineSegment(sketch, "E115.left", {"start": v(-72.33, -47.93) * mm, "end": v(-72.33, -37.93) * mm});
            skLineSegment(sketch, "E115.right", {"start": v(-71.33, -47.93) * mm, "end": v(-71.33, -37.93) * mm});
            skLineSegment(sketch, "E116.bottom", {"start": v(80.61, 38.46) * mm, "end": v(81.61, 38.46) * mm});
            skLineSegment(sketch, "E116.top", {"start": v(80.61, 48.46) * mm, "end": v(81.61, 48.46) * mm});
            skLineSegment(sketch, "E116.left", {"start": v(80.61, 38.46) * mm, "end": v(80.61, 48.46) * mm});
            skLineSegment(sketch, "E116.right", {"start": v(81.61, 38.46) * mm, "end": v(81.61, 48.46) * mm});
            skLineSegment(sketch, "E117.bottom", {"start": v(73.9, 150.32) * mm, "end": v(74.9, 150.32) * mm});
            skLineSegment(sketch, "E117.top", {"start": v(73.9, 160.32) * mm, "end": v(74.9, 160.32) * mm});
            skLineSegment(sketch, "E117.left", {"start": v(73.9, 150.32) * mm, "end": v(73.9, 160.32) * mm});
            skLineSegment(sketch, "E117.right", {"start": v(74.9, 150.32) * mm, "end": v(74.9, 160.32) * mm});
            skLineSegment(sketch, "E118.bottom", {"start": v(124.5, 143.1) * mm, "end": v(125.5, 143.1) * mm});
            skLineSegment(sketch, "E118.top", {"start": v(124.5, 153.1) * mm, "end": v(125.5, 153.1) * mm});
            skLineSegment(sketch, "E118.left", {"start": v(124.5, 143.1) * mm, "end": v(124.5, 153.1) * mm});
            skLineSegment(sketch, "E118.right", {"start": v(125.5, 143.1) * mm, "end": v(125.5, 153.1) * mm});
            skLineSegment(sketch, "E119.bottom", {"start": v(-44.87, 180.83) * mm, "end": v(-43.87, 180.83) * mm});
            skLineSegment(sketch, "E119.top", {"start": v(-44.87, 190.83) * mm, "end": v(-43.87, 190.83) * mm});
            skLineSegment(sketch, "E119.left", {"start": v(-44.87, 180.83) * mm, "end": v(-44.87, 190.83) * mm});
            skLineSegment(sketch, "E119.right", {"start": v(-43.87, 180.83) * mm, "end": v(-43.87, 190.83) * mm});
            skLineSegment(sketch, "E120.bottom", {"start": v(-1.1, 220.88) * mm, "end": v(-0.1, 220.88) * mm});
            skLineSegment(sketch, "E120.top", {"start": v(-1.1, 230.88) * mm, "end": v(-0.1, 230.88) * mm});
            skLineSegment(sketch, "E120.left", {"start": v(-1.1, 220.88) * mm, "end": v(-1.1, 230.88) * mm});
            skLineSegment(sketch, "E120.right", {"start": v(-0.1, 220.88) * mm, "end": v(-0.1, 230.88) * mm});
            skLineSegment(sketch, "E121.bottom", {"start": v(19.32, -397.64) * mm, "end": v(20.32, -397.64) * mm});
            skLineSegment(sketch, "E121.top", {"start": v(19.32, -387.64) * mm, "end": v(20.32, -387.64) * mm});
            skLineSegment(sketch, "E121.left", {"start": v(19.32, -397.64) * mm, "end": v(19.32, -387.64) * mm});
            skLineSegment(sketch, "E121.right", {"start": v(20.32, -397.64) * mm, "end": v(20.32, -387.64) * mm});
            skLineSegment(sketch, "E122.bottom", {"start": v(-49.52, -366.01) * mm, "end": v(-48.52, -366.01) * mm});
            skLineSegment(sketch, "E122.top", {"start": v(-49.52, -356.01) * mm, "end": v(-48.52, -356.01) * mm});
            skLineSegment(sketch, "E122.left", {"start": v(-49.52, -366.01) * mm, "end": v(-49.52, -356.01) * mm});
            skLineSegment(sketch, "E122.right", {"start": v(-48.52, -366.01) * mm, "end": v(-48.52, -356.01) * mm});
            skLineSegment(sketch, "E123.bottom", {"start": v(-31.45, 331.22) * mm, "end": v(-30.45, 331.22) * mm});
            skLineSegment(sketch, "E123.top", {"start": v(-31.45, 341.22) * mm, "end": v(-30.45, 341.22) * mm});
            skLineSegment(sketch, "E123.left", {"start": v(-31.45, 331.22) * mm, "end": v(-31.45, 341.22) * mm});
            skLineSegment(sketch, "E123.right", {"start": v(-30.45, 331.22) * mm, "end": v(-30.45, 341.22) * mm});
            skLineSegment(sketch, "E124.bottom", {"start": v(-27.84, 410.44) * mm, "end": v(-26.84, 410.44) * mm});
            skLineSegment(sketch, "E124.top", {"start": v(-27.84, 420.44) * mm, "end": v(-26.84, 420.44) * mm});
            skLineSegment(sketch, "E124.left", {"start": v(-27.84, 410.44) * mm, "end": v(-27.84, 420.44) * mm});
            skLineSegment(sketch, "E124.right", {"start": v(-26.84, 410.44) * mm, "end": v(-26.84, 420.44) * mm});
            skLineSegment(sketch, "E125.bottom", {"start": v(-50.61, 336.77) * mm, "end": v(-49.61, 336.77) * mm});
            skLineSegment(sketch, "E125.top", {"start": v(-50.61, 346.77) * mm, "end": v(-49.61, 346.77) * mm});
            skLineSegment(sketch, "E125.left", {"start": v(-50.61, 336.77) * mm, "end": v(-50.61, 346.77) * mm});
            skLineSegment(sketch, "E125.right", {"start": v(-49.61, 336.77) * mm, "end": v(-49.61, 346.77) * mm});
            skLineSegment(sketch, "E126.bottom", {"start": v(77.86, -22.14) * mm, "end": v(78.86, -22.14) * mm});
            skLineSegment(sketch, "E126.top", {"start": v(77.86, -12.14) * mm, "end": v(78.86, -12.14) * mm});
            skLineSegment(sketch, "E126.left", {"start": v(77.86, -22.14) * mm, "end": v(77.86, -12.14) * mm});
            skLineSegment(sketch, "E126.right", {"start": v(78.86, -22.14) * mm, "end": v(78.86, -12.14) * mm});
            skLineSegment(sketch, "E127.bottom", {"start": v(-104.96, -85.6) * mm, "end": v(-103.96, -85.6) * mm});
            skLineSegment(sketch, "E127.top", {"start": v(-104.96, -75.6) * mm, "end": v(-103.96, -75.6) * mm});
            skLineSegment(sketch, "E127.left", {"start": v(-104.96, -85.6) * mm, "end": v(-104.96, -75.6) * mm});
            skLineSegment(sketch, "E127.right", {"start": v(-103.96, -85.6) * mm, "end": v(-103.96, -75.6) * mm});
            skLineSegment(sketch, "E128.bottom", {"start": v(-55.07, 78.32) * mm, "end": v(-54.07, 78.32) * mm});
            skLineSegment(sketch, "E128.top", {"start": v(-55.07, 88.32) * mm, "end": v(-54.07, 88.32) * mm});
            skLineSegment(sketch, "E128.left", {"start": v(-55.07, 78.32) * mm, "end": v(-55.07, 88.32) * mm});
            skLineSegment(sketch, "E128.right", {"start": v(-54.07, 78.32) * mm, "end": v(-54.07, 88.32) * mm});
            skLineSegment(sketch, "E129.bottom", {"start": v(4, 121.8) * mm, "end": v(5, 121.8) * mm});
            skLineSegment(sketch, "E129.top", {"start": v(4, 131.8) * mm, "end": v(5, 131.8) * mm});
            skLineSegment(sketch, "E129.left", {"start": v(4, 121.8) * mm, "end": v(4, 131.8) * mm});
            skLineSegment(sketch, "E129.right", {"start": v(5, 121.8) * mm, "end": v(5, 131.8) * mm});
            skLineSegment(sketch, "E130.bottom", {"start": v(-10.63, -146.13) * mm, "end": v(-9.63, -146.13) * mm});
            skLineSegment(sketch, "E130.top", {"start": v(-10.63, -136.13) * mm, "end": v(-9.63, -136.13) * mm});
            skLineSegment(sketch, "E130.left", {"start": v(-10.63, -146.13) * mm, "end": v(-10.63, -136.13) * mm});
            skLineSegment(sketch, "E130.right", {"start": v(-9.63, -146.13) * mm, "end": v(-9.63, -136.13) * mm});
            skLineSegment(sketch, "E131.bottom", {"start": v(60.73, -224.07) * mm, "end": v(61.73, -224.07) * mm});
            skLineSegment(sketch, "E131.top", {"start": v(60.73, -214.07) * mm, "end": v(61.73, -214.07) * mm});
            skLineSegment(sketch, "E131.left", {"start": v(60.73, -224.07) * mm, "end": v(60.73, -214.07) * mm});
            skLineSegment(sketch, "E131.right", {"start": v(61.73, -224.07) * mm, "end": v(61.73, -214.07) * mm});
            skSolve(sketch);
        }
        {
            var Q0;
            Q0=qSketchRegion(id+"F5",true);
            extrude(context, id + "F6", {"entities" : qUnion([Q0]), "oppositeDirection" : true, "depth" : 800 * mm});
        }
        {
            var Q0;
            Q0=qCreatedBy(makeId("Top.planeOp"),FACE);
            var sketch = newSketch(context, id + "F7", { "sketchPlane" : qUnion([Q0])});
            skLineSegment(sketch, "E132.bottom", {"start": v(200, 500) * mm, "end": v(-200, 500) * mm});
            skLineSegment(sketch, "E132.top", {"start": v(200, -500) * mm, "end": v(-200, -500) * mm});
            skLineSegment(sketch, "E132.left", {"start": v(200, 500) * mm, "end": v(200, -500) * mm});
            skLineSegment(sketch, "E132.right", {"start": v(-200, 500) * mm, "end": v(-200, -500) * mm});
            skPoint(sketch, "E132.middle", {"position": v(0, 0) * mm});
            skSolve(sketch);
        }
        {
            var Q0;
            Q0=qSketchRegion(id+"F7",true);
            extrude(context, id + "F8", {"entities" : qUnion([Q0]), "depth" : 10 * mm});
        }
        {
            var Q0;
            Q0=qCreatedBy(makeId("Top.planeOp"),FACE);
            var sketch = newSketch(context, id + "F9", { "sketchPlane" : qUnion([Q0])});
            skLineSegment(sketch, "E133.bottom", {"start": v(185.04, -448.96) * mm, "end": v(-164.96, -448.96) * mm});
            skLineSegment(sketch, "E133.top", {"start": v(185.04, 451.04) * mm, "end": v(-164.96, 451.04) * mm});
            skLineSegment(sketch, "E133.left", {"start": v(185.04, -448.96) * mm, "end": v(185.04, 451.04) * mm});
            skLineSegment(sketch, "E133.right", {"start": v(-164.96, -448.96) * mm, "end": v(-164.96, 451.04) * mm});
            skPoint(sketch, "E133.middle", {"position": v(10.04, 1.04) * mm});
            skSolve(sketch);
        }
        {
            var Q0;
            Q0=makeQuery(id+"F9.imprint","IMPRINT",FACE,{"disambiguationData":[TD([[makeQuery(id+"F9.imprint","IMPRINT",EDGE,{"derivedFrom":sQuery(id+"F9.wireOp",EDGE,"E133.bottom")}),-1.0]])]});
            extrude(context, id + "F10", {"entities" : qUnion([Q0]), "depth" : 10 * mm});
        }
        {
            var Q0;
            Q0=makeQuery(id+"F10.opExtrude","CAP_FACE",FACE,{"disambiguationData":[OSD([sQuery(id+"F9.wireOp",EDGE,"E133.bottom"),sQuery(id+"F9.wireOp",EDGE,"E133.top"),sQuery(id+"F9.wireOp",EDGE,"E133.left"),sQuery(id+"F9.wireOp",EDGE,"E133.right")])],"isStart":true});
            shell(context, id + "F11", {"entities" : qUnion([Q0]), "thickness" : 10 * mm, "oppositeDirection" : true});
        }
    });
